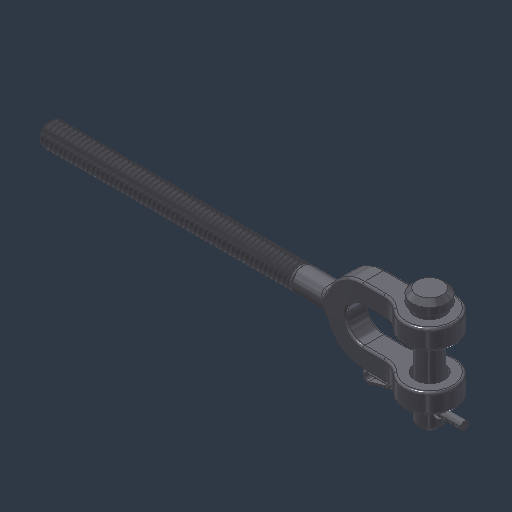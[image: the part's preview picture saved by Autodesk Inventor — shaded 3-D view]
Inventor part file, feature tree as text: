
AUTODESK INVENTOR PART (.ipt)
format: ipt  version: 2024.3 (Build 283343000, 343)  size: 1,122,304 bytes
history: native  units: mm (DEFAULTED — no unit token found)
features: other x2, fillet x1
ambient origin geometry x8: Origin, YZ Plane, XZ Plane, XY Plane, X Axis, Y Axis, Z Axis, Center Point
bodies: Solid1 (feature_tree), Solid2 (feature_tree), Solid3 (feature_tree)
feature tree (3):
  other  "Split Line1"
  fillet  "Fillet3"  [1 undecoded]
  other  "Boss-Extrude1"
note: 1 required parameter value undecoded (feature->parameter linkage not recoverable at this tier; creation-order binding heuristic only, values carry confidence <= 0.55)
